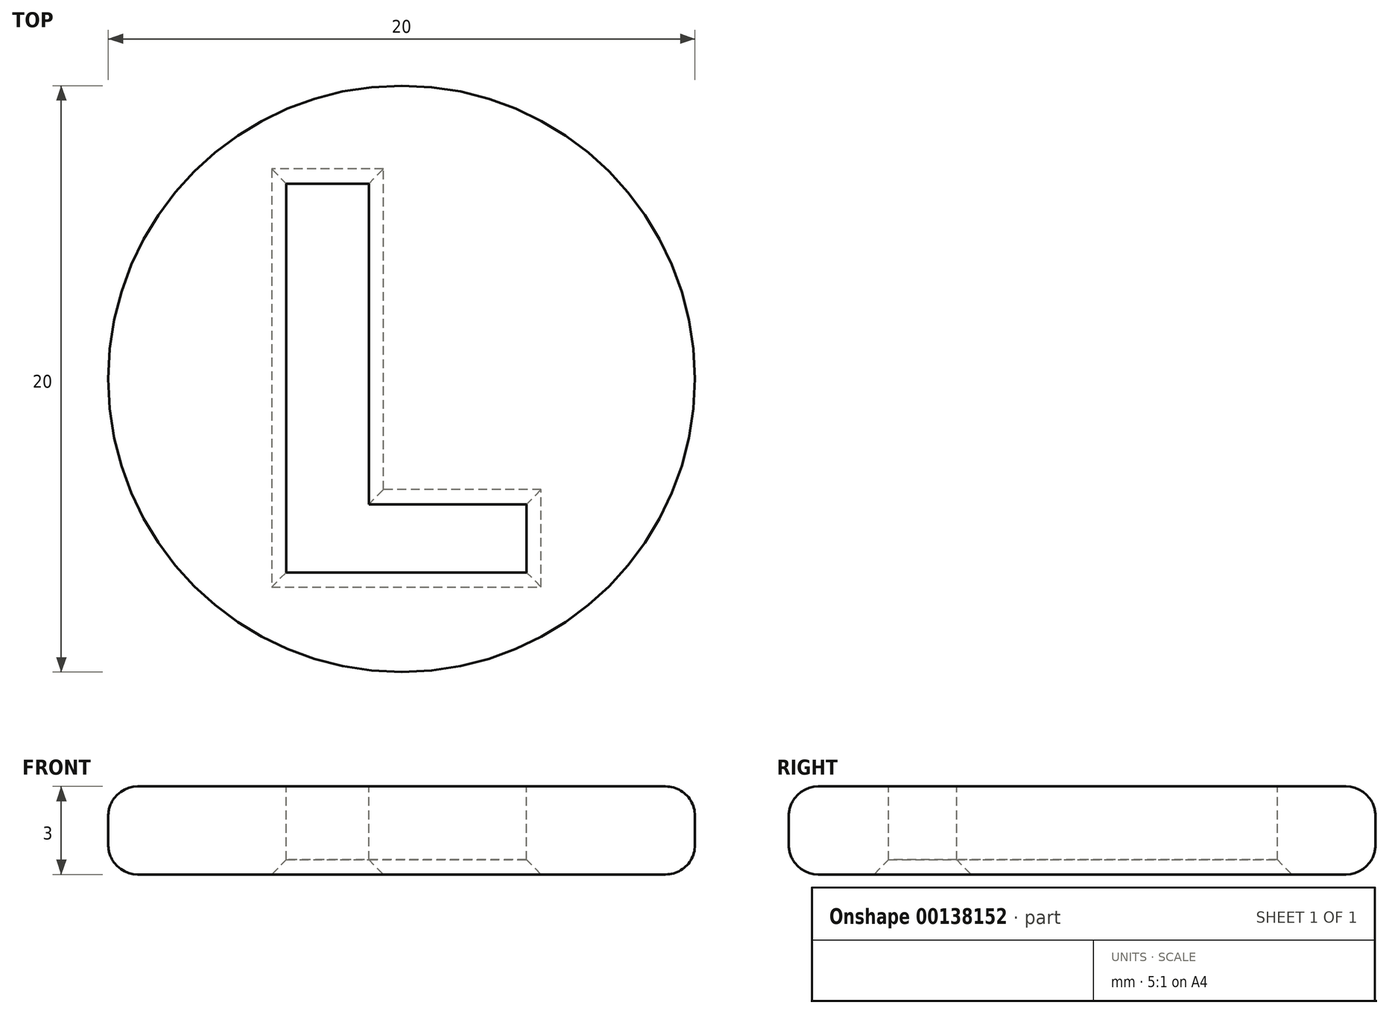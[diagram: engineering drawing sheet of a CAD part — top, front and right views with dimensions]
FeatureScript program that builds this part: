
annotation { "Feature Type Name" : "Feature", "Feature Type Description" : "" }
export const myFeature = defineFeature(function(context is Context, id is Id, definition is map)
    precondition{}
    {
        {
            var Q0;
            Q0=qCreatedBy(makeId("Top.planeOp"),FACE);
            var sketch = newSketch(context, id + "F0", { "sketchPlane" : qUnion([Q0])});
            skCircle(sketch, "E0", {"center": v(0, 0) * mm, "radius": 10 * mm});
            skSolve(sketch);
        }
        {
            var Q0;
            Q0 = qSketchRegion(id + "F0", true);
            extrude(context, id + "F1", {"entities" : qUnion([Q0]), "depth" : 3 * mm});
        }
        {
            var Q0;
            Q0=makeQuery(id+"F1.opExtrude","CAP_EDGE",EDGE,{"disambiguationData":[OSD([sQuery(id+"F0.wireOp",EDGE,"E0")])],"isStart":false});
            var Q1;
            Q1=makeQuery(id+"F1.opExtrude","CAP_EDGE",EDGE,{"disambiguationData":[OSD([sQuery(id+"F0.wireOp",EDGE,"E0")])],"isStart":true});
            fillet(context, id + "F2", {"entities" : qUnion([Q0, Q1]), "radius" : 1 * mm, "tangentPropagation" : true, "allowEdgeOverflow" : false});
        }
        {
            var Q0;
            Q0=makeQuery(id+"F1.opExtrude","CAP_FACE",FACE,{"disambiguationData":[OSD([sQuery(id+"F0.wireOp",EDGE,"E0")])],"isStart":false});
            var sketch = newSketch(context, id + "F3", { "sketchPlane" : qUnion([Q0])});
            skText(sketch, "E1", { "text": "L", "fontName": "OpenSans-Bold.ttf"});
            const initialGuessF3  = {"E1": [-0.0056, -0.0066, 1, 0, 0.01337]};
            skSetInitialGuess(sketch, initialGuessF3);
            skSolve(sketch);
        }
        {
            var Q0;
            Q0 = qSketchRegion(id + "F3", true);
            extrude(context, id + "F4", {"entities" : qUnion([Q0]), "operationType" : NewBodyOperationType.REMOVE, "oppositeDirection" : true, "depth" : 6 * mm});
        }
        {
            var Q0;
            Q0=makeQuery(id+"F4.boolean.opBoolean","COPY",EDGE,{"derivedFrom":makeQuery(id+"F4.opExtrude","CAP_EDGE",EDGE,{"disambiguationData":[OSD([sQuery(id+"F3.wireOp",EDGE,"E1.sketch_text.stroke-0")])],"isStart":true})});
            var Q1;
            Q1=makeQuery(id+"F4.boolean.opBoolean","COPY",EDGE,{"derivedFrom":makeQuery(id+"F4.opExtrude","CAP_EDGE",EDGE,{"disambiguationData":[OSD([sQuery(id+"F3.wireOp",EDGE,"E1.sketch_text.stroke-2")])],"isStart":true})});
            var Q2;
            Q2=makeQuery(id+"F4.boolean.opBoolean","COPY",EDGE,{"derivedFrom":makeQuery(id+"F4.opExtrude","CAP_EDGE",EDGE,{"disambiguationData":[OSD([sQuery(id+"F3.wireOp",EDGE,"E1.sketch_text.stroke-3")])],"isStart":true})});
            var Q3;
            Q3=makeQuery(id+"F4.boolean.opBoolean","COPY",EDGE,{"derivedFrom":makeQuery(id+"F4.opExtrude","CAP_EDGE",EDGE,{"disambiguationData":[OSD([sQuery(id+"F3.wireOp",EDGE,"E1.sketch_text.stroke-1")])],"isStart":true})});
            var Q4;
            Q4=makeQuery(id+"F4.boolean.opBoolean","COPY",EDGE,{"derivedFrom":makeQuery(id+"F4.opExtrude","CAP_EDGE",EDGE,{"disambiguationData":[OSD([sQuery(id+"F3.wireOp",EDGE,"E1.sketch_text.stroke-5")])],"isStart":true})});
            var Q5;
            Q5=makeQuery(id+"F4.boolean.opBoolean","COPY",EDGE,{"derivedFrom":makeQuery(id+"F4.opExtrude","CAP_EDGE",EDGE,{"disambiguationData":[OSD([sQuery(id+"F3.wireOp",EDGE,"E1.sketch_text.stroke-4")])],"isStart":true})});
            var Q6;
            Q6=makeQuery(id+"F4.boolean.opBoolean","INTERSECT",EDGE,{"derivedFrom":[makeQuery(id+"F1.opExtrude","CAP_FACE",FACE,{"disambiguationData":[OSD([sQuery(id+"F0.wireOp",EDGE,"E0")])],"isStart":true}),makeQuery(id+"F4.opExtrude","SWEPT_FACE",FACE,{"disambiguationData":[OSD([sQuery(id+"F3.wireOp",EDGE,"E1.sketch_text.stroke-2")])]})]});
            var Q7;
            Q7=makeQuery(id+"F4.boolean.opBoolean","INTERSECT",EDGE,{"derivedFrom":[makeQuery(id+"F1.opExtrude","CAP_FACE",FACE,{"disambiguationData":[OSD([sQuery(id+"F0.wireOp",EDGE,"E0")])],"isStart":true}),makeQuery(id+"F4.opExtrude","SWEPT_FACE",FACE,{"disambiguationData":[OSD([sQuery(id+"F3.wireOp",EDGE,"E1.sketch_text.stroke-1")])]})]});
            var Q8;
            Q8=makeQuery(id+"F1.opExtrude","CAP_FACE",FACE,{"disambiguationData":[OSD([sQuery(id+"F0.wireOp",EDGE,"E0")])],"isStart":true});
            chamfer(context, id + "F5", {"entities" : qUnion([Q0, Q1, Q2, Q3, Q4, Q5, Q6, Q7, Q8]), "width" : .5 * mm, "tangentPropagation" : true});
        }
    });
